# Revit family: NLRS_57_DUF_UN_instortkanaal-rechthoekig-naar-rond-verloop_LT_velu
name_source: partatom
category: Duct Fittings
units: mm (PartAtom-declared; Revit-internal decimal feet)

## family parameters
Always vertical = Yes
Cut with Voids When Loaded = No
Part Type = Transition
Round Connector Dimension = Use Diameter
Shared = No
Work Plane-Based = No

## types (3) — shared parameters
Assembly Code = 57.00
Description = Velu Instort Kanaal: rechthoekig naar rond verloop
Manufacturer = Velu Klimaattechnische Groothandel
Model = VIK rechthoekig naar rond
NLRS_C_content_datum_gewijzigd = 18-01-2023
NLRS_C_content_provider = Velu Klimaattechnische Groothandel
NLRS_C_content_versie = 3.20.01
NLRS_C_description = Velu Instort Kanaal: rechthoekig naar rond verloop
Type Comments = Enkel geschikt voor VELU instort kanaal maten
URL = https://webshop.velu.nl
VELU_Article_Data = RHOR
VELU_Centerline = Yes
zero-valued in all types: Default Elevation

## per-type parameters (varying)
| type | VELU_Product_Selector | VELU_Show_Center_Type1 | VELU_Show_Center_Type2 | VELU_Show_Type1 | VELU_Show_Type2 |
| BZV (brede zijde vlak) | 2 | No | Yes | No | Yes |
| SZV (smalle zijde vlak) | 3 | Yes | No | Yes | No |
| SYM (hart=hart) | 1 | Yes | No | Yes | No |

## geometry (parser evidence)
native form markers: Sweep x3
no freeform markers — native parametric forms only
